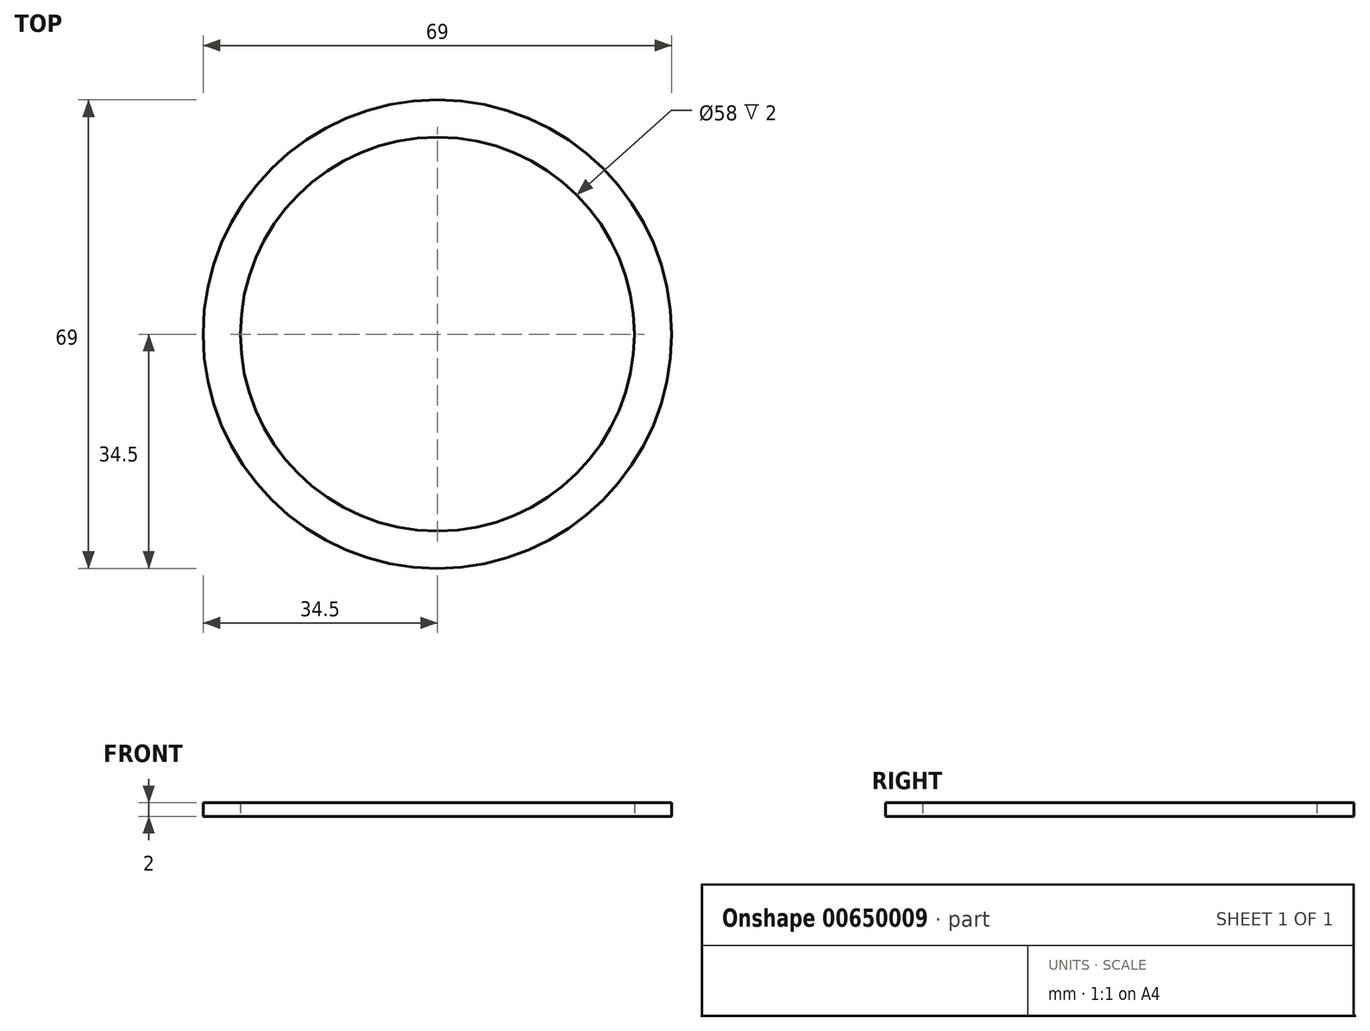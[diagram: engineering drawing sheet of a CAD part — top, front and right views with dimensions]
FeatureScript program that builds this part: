
annotation { "Feature Type Name" : "Feature", "Feature Type Description" : "" }
export const myFeature = defineFeature(function(context is Context, id is Id, definition is map)
    precondition{}
    {
        {
            var Q0;
            Q0=qCreatedBy(makeId("Top.planeOp"),FACE);
            var sketch = newSketch(context, id + "F0", { "sketchPlane" : qUnion([Q0])});
            skCircle(sketch, "E0", {"center": v(0, 0) * mm, "radius": 34.5 * mm});
            skCircle(sketch, "E1", {"center": v(0, 0) * mm, "radius": 28.25 * mm, "construction": true});
            skCircle(sketch, "E2", {"center": v(0, 0) * mm, "radius": 29 * mm});
            skSolve(sketch);
        }
        {
            var Q0;
            Q0=makeQuery(id+"F0.imprint","IMPRINT",FACE,{"disambiguationData":[TD([[makeQuery(id+"F0.imprint","IMPRINT",EDGE,{"derivedFrom":sQuery(id+"F0.wireOp",EDGE,"E0")}),1.0]])]});
            extrude(context, id + "F1", {"entities" : qUnion([Q0]), "depth" : 2 * mm, "offsetDistance" : 25 * mm});
        }
    });
